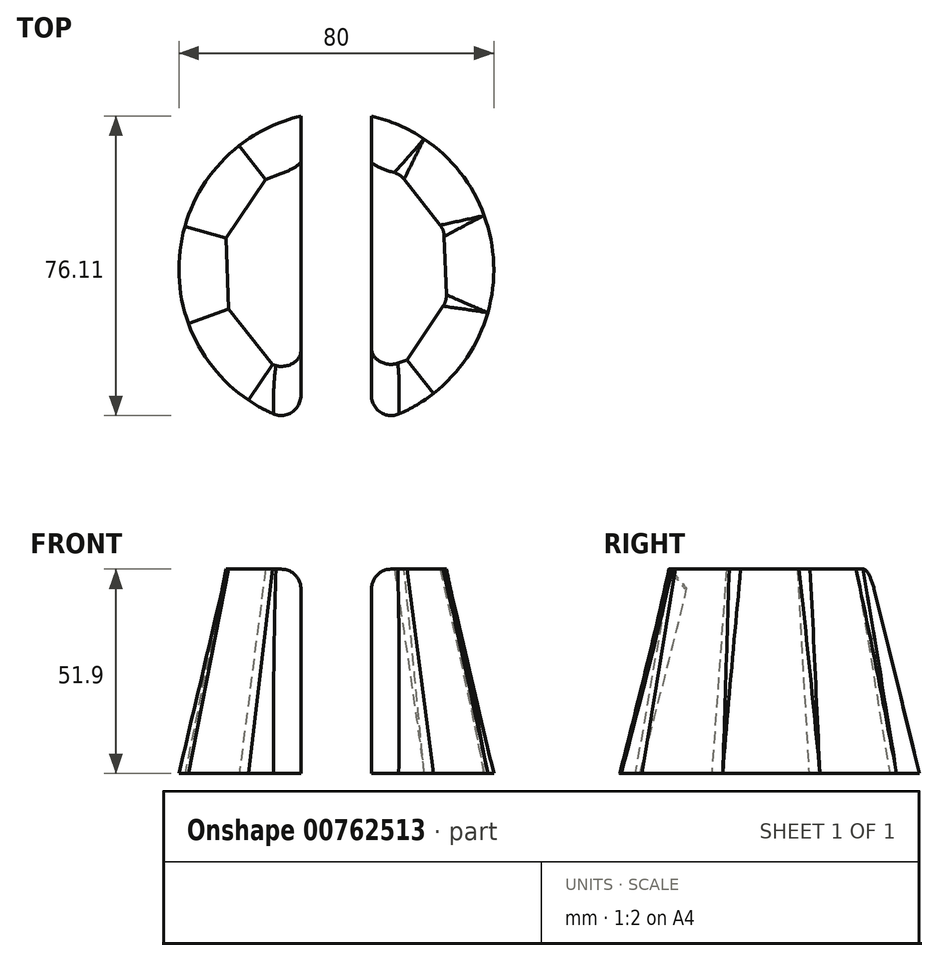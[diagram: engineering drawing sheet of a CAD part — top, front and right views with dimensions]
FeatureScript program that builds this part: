
annotation { "Feature Type Name" : "Feature", "Feature Type Description" : "" }
export const myFeature = defineFeature(function(context is Context, id is Id, definition is map)
    precondition{}
    {
        {
            var Q0;
            Q0=qCreatedBy(makeId("Top.planeOp"),FACE);
            var sketch = newSketch(context, id + "F0", { "sketchPlane" : qUnion([Q0])});
            skCircle(sketch, "E0", {"center": v(0, 0) * mm, "radius": 40 * mm});
            skSolve(sketch);
        }
        {
            var Q0;
            Q0=qCreatedBy(makeId("Top.planeOp"),FACE);
            cPlane(context, id + "F1", {"entities" : qUnion([Q0]), "cplaneType" : CPlaneType.OFFSET, "offset" : 51.9 * mm, "width" : 150 * mm, "height" : 150 * mm});
        }
        {
            var Q0;
            Q0=qCreatedBy(id+"F1.planeOp",FACE);
            var sketch = newSketch(context, id + "F2", { "sketchPlane" : qUnion([Q0])});
            skCircle(sketch, "E1.cCircle", {"center": v(0, 0) * mm, "radius": 27.7 * mm, "construction": true});
            skLineSegment(sketch, "E1.0", {"start": v(28.01, -7.98) * mm, "end": v(17.97, -22.92) * mm});
            skLineSegment(sketch, "E1.1", {"start": v(17.97, -22.92) * mm, "end": v(1.07, -29.1) * mm});
            skLineSegment(sketch, "E1.2", {"start": v(1.07, -29.1) * mm, "end": v(-16.25, -24.18) * mm});
            skLineSegment(sketch, "E1.3", {"start": v(-16.25, -24.18) * mm, "end": v(-27.35, -10.01) * mm});
            skLineSegment(sketch, "E1.4", {"start": v(-27.35, -10.01) * mm, "end": v(-28.01, 7.98) * mm});
            skLineSegment(sketch, "E1.5", {"start": v(-28.01, 7.98) * mm, "end": v(-17.97, 22.92) * mm});
            skLineSegment(sketch, "E1.6", {"start": v(-17.97, 22.92) * mm, "end": v(-1.07, 29.1) * mm});
            skLineSegment(sketch, "E1.7", {"start": v(-1.07, 29.1) * mm, "end": v(16.25, 24.18) * mm});
            skLineSegment(sketch, "E1.8", {"start": v(16.25, 24.18) * mm, "end": v(27.35, 10.01) * mm});
            skLineSegment(sketch, "E1.9", {"start": v(27.35, 10.01) * mm, "end": v(28.01, -7.98) * mm});
            skPoint(sketch, "E1.0.midPoint", {"position": v(23, -15.45) * mm});
            skSolve(sketch);
        }
        {
            var Q0;
            Q0=makeQuery(id+"F2.imprint","IMPRINT",FACE,{"disambiguationData":[TD([[makeQuery(id+"F2.imprint","IMPRINT",EDGE,{"derivedFrom":sQuery(id+"F2.wireOp",EDGE,"E1.0")}),-1.0]])]});
            var Q1;
            Q1=makeQuery(id+"F0.imprint","IMPRINT",FACE,{"disambiguationData":[TD([[makeQuery(id+"F0.imprint","IMPRINT",EDGE,{"derivedFrom":sQuery(id+"F0.wireOp",EDGE,"E0")}),1.0]])]});
            loft(context, id + "F3", {"sheetProfilesArray" : [{ "sheetProfileEntities" : qUnion([Q0]) }, { "sheetProfileEntities" : qUnion([Q1]) }]});
        }
        {
            var Q0;
            Q0=qCreatedBy(makeId("Front.planeOp"),FACE);
            cPlane(context, id + "F4", {"entities" : qUnion([Q0]), "cplaneType" : CPlaneType.OFFSET, "offset" : 41.5 * mm, "oppositeDirection" : true, "width" : 150 * mm, "height" : 150 * mm});
        }
        {
            var Q0;
            Q0=qCreatedBy(id+"F4.planeOp",FACE);
            var sketch = newSketch(context, id + "F5", { "sketchPlane" : qUnion([Q0])});
            skLineSegment(sketch, "E2.bottom", {"start": v(-9, 54.14) * mm, "end": v(8.93, 54.14) * mm});
            skLineSegment(sketch, "E2.top", {"start": v(-9, -4.23) * mm, "end": v(8.93, -4.23) * mm});
            skLineSegment(sketch, "E2.left", {"start": v(-9, 54.14) * mm, "end": v(-9, -4.23) * mm});
            skLineSegment(sketch, "E2.right", {"start": v(8.93, 54.14) * mm, "end": v(8.93, -4.23) * mm});
            skSolve(sketch);
        }
        {
            var Q0;
            Q0=makeQuery(id+"F5.imprint","IMPRINT",FACE,{"disambiguationData":[TD([[makeQuery(id+"F5.imprint","IMPRINT",EDGE,{"derivedFrom":sQuery(id+"F5.wireOp",EDGE,"E2.bottom")}),-1.0]])]});
            extrude(context, id + "F6", {"entities" : qUnion([Q0]), "operationType" : NewBodyOperationType.REMOVE, "depth" : 92.8 * mm, "offsetDistance" : 25 * mm});
        }
        {
            var Q0;
            Q0=makeQuery(id+"F6.boolean.opBoolean","INTERSECT",EDGE,{"derivedFrom":[makeQuery(id+"F3.opLoft","CAP_FACE",FACE,{"disambiguationData":[OSD([makeQuery(id+"F2.imprint","IMPRINT",FACE,{"disambiguationData":[TD([[makeQuery(id+"F2.imprint","IMPRINT",EDGE,{"derivedFrom":sQuery(id+"F2.wireOp",EDGE,"E1.0")}),-1.0]])]})])],"isStart":true}),makeQuery(id+"F6.opExtrude","SWEPT_FACE",FACE,{"disambiguationData":[OSD([sQuery(id+"F5.wireOp",EDGE,"E2.left")])]})]});
            var Q1;
            Q1=makeQuery(id+"F6.boolean.opBoolean","INTERSECT",EDGE,{"derivedFrom":[makeQuery(id+"F3.opLoft","CAP_FACE",FACE,{"disambiguationData":[OSD([makeQuery(id+"F2.imprint","IMPRINT",FACE,{"disambiguationData":[TD([[makeQuery(id+"F2.imprint","IMPRINT",EDGE,{"derivedFrom":sQuery(id+"F2.wireOp",EDGE,"E1.0")}),-1.0]])]})])],"isStart":true}),makeQuery(id+"F6.opExtrude","SWEPT_FACE",FACE,{"disambiguationData":[OSD([sQuery(id+"F5.wireOp",EDGE,"E2.right")])]})]});
            var Q2;
            Q2=makeQuery(id+"F6.boolean.opBoolean","INTERSECT",EDGE,{"derivedFrom":[makeQuery(id+"F3.opLoft","SWEPT_FACE",FACE,{"disambiguationData":[OSD([sQuery(id+"F0.wireOp",EDGE,"E0"),sQuery(id+"F2.wireOp",EDGE,"E1.0"),sQuery(id+"F2.wireOp",EDGE,"E1.1"),sQuery(id+"F2.wireOp",EDGE,"E1.2"),sQuery(id+"F2.wireOp",EDGE,"E1.3")])]}),makeQuery(id+"F6.opExtrude","SWEPT_FACE",FACE,{"disambiguationData":[OSD([sQuery(id+"F5.wireOp",EDGE,"E2.left")])]})]});
            var Q3;
            Q3=makeQuery(id+"F6.boolean.opBoolean","INTERSECT",EDGE,{"derivedFrom":[makeQuery(id+"F3.opLoft","SWEPT_FACE",FACE,{"disambiguationData":[OSD([sQuery(id+"F0.wireOp",EDGE,"E0"),sQuery(id+"F2.wireOp",EDGE,"E1.0"),sQuery(id+"F2.wireOp",EDGE,"E1.1"),sQuery(id+"F2.wireOp",EDGE,"E1.2"),sQuery(id+"F2.wireOp",EDGE,"E1.9")])]}),makeQuery(id+"F6.opExtrude","SWEPT_FACE",FACE,{"disambiguationData":[OSD([sQuery(id+"F5.wireOp",EDGE,"E2.right")])]})]});
            var Q4;
            Q4=makeQuery(id+"F3.opLoft","SWEPT_EDGE",EDGE,{"disambiguationData":[OSD([sQuery(id+"F0.wireOp",EDGE,"E0"),sQuery(id+"F2.wireOp",EDGE,"E1.0"),sQuery(id+"F2.wireOp",EDGE,"E1.1"),sQuery(id+"F2.wireOp",EDGE,"E1.9")])]});
            var Q5;
            Q5=makeQuery(id+"F3.opLoft","SWEPT_EDGE",EDGE,{"disambiguationData":[OSD([sQuery(id+"F2.wireOp",EDGE,"E1.0"),sQuery(id+"F2.wireOp",EDGE,"E1.9")])]});
            var Q6;
            Q6=makeQuery(id+"F3.opLoft","SWEPT_EDGE",EDGE,{"disambiguationData":[OSD([sQuery(id+"F0.wireOp",EDGE,"E0"),sQuery(id+"F2.wireOp",EDGE,"E1.7"),sQuery(id+"F2.wireOp",EDGE,"E1.8"),sQuery(id+"F2.wireOp",EDGE,"E1.9")])]});
            fillet(context, id + "F7", {"entities" : qUnion([Q0, Q1, Q2, Q3, Q4, Q5, Q6]), "radius" : 5 * mm, "tangentPropagation" : true, "allowEdgeOverflow" : false});
        }
    });
